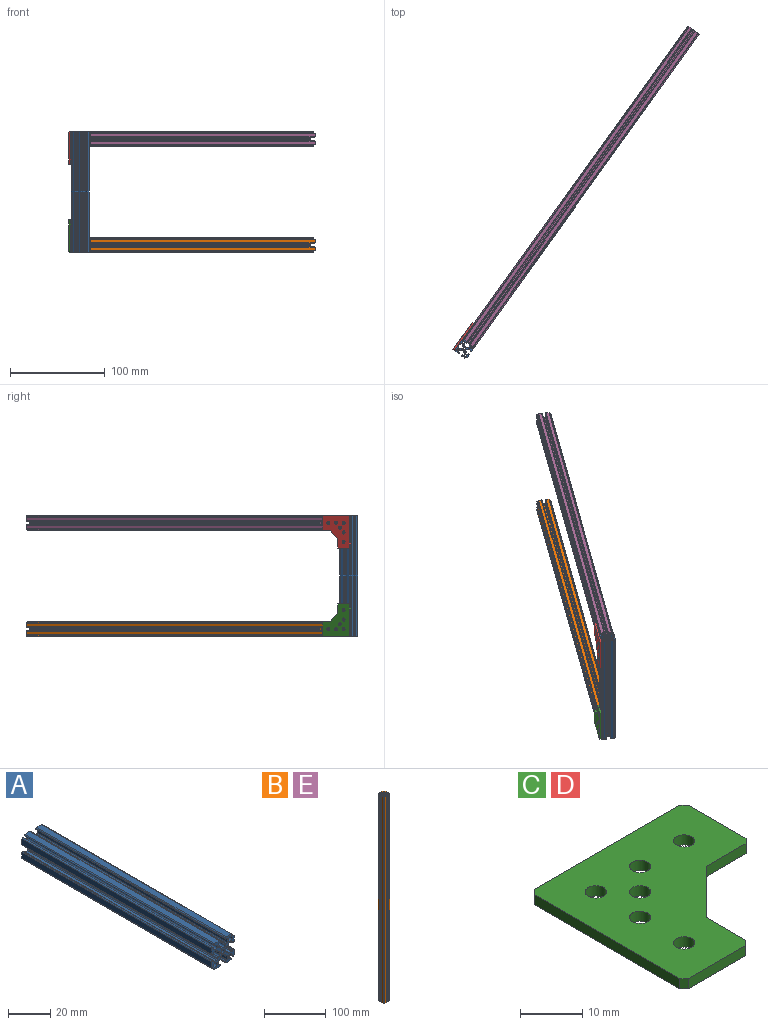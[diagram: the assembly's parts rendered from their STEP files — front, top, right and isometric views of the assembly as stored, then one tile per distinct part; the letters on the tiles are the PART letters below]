
ASSEMBLY  parts=5 mates=12
PART A: 115 faces, bbox 15x127x15 mm
  f0: plane 127x3.34mm, normal (1,0,0), area 423.7mm2, adj f23,f70,f112,f114
  f1: plane 127x3.34mm, normal (0,0,-1), area 423.7mm2, adj f16,f23,f77,f114
  f2: plane 127x3.34mm, normal (-1,0,0), area 423.7mm2, adj f23,f58,f109,f114
  f3: plane 127x3.34mm, normal (0,0,1), area 423.7mm2, adj f23,f65,f111,f114
  f4: plane 127x3.34mm, normal (-1,0,0), area 423.7mm2, adj f23,f62,f113,f114
  f5: plane 127x3.34mm, normal (0,0,-1), area 423.7mm2, adj f17,f23,f73,f114
  f6: plane 127x3.34mm, normal (1,0,0), area 423.7mm2, adj f23,f69,f110,f114
  f7: plane 127x3.34mm, normal (0,0,1), area 423.7mm2, adj f23,f63,f108,f114
  f8: plane 127x0.2mm, normal (-1,0,0), area 25.4mm2, adj f23,f65,f66,f114
  f9: plane 127x0.2mm, normal (1,0,0), area 25.4mm2, adj f23,f63,f64,f114
  f10: plane 127x0.2mm, normal (0,0,-1), area 25.4mm2, adj f23,f58,f59,f114
  f11: plane 127x0.2mm, normal (0,0,1), area 25.4mm2, adj f23,f61,f62,f114
  f12: plane 127x0.2mm, normal (1,0,0), area 25.4mm2, adj f23,f76,f77,f114
  f13: plane 127x0.2mm, normal (-1,0,0), area 25.4mm2, adj f23,f73,f74,f114
  f14: plane 127x0.2mm, normal (0,0,1), area 25.4mm2, adj f23,f70,f71,f114
  f15: plane 127x0.2mm, normal (0,0,-1), area 25.4mm2, adj f23,f68,f69,f114
  f16: cylinder r=0.5mm len=127mm, axis (0,1,0), area 149.6mm2, adj f1,f23,f53,f114
  f17: cylinder r=0.5mm len=127mm, axis (0,-1,0), area 149.6mm2, adj f5,f23,f102,f114
  f18: cylinder r=1.25mm len=127mm, axis (0,1,0), area 866.8mm2, adj f23,f104,f105,f114
  f19: cylinder r=1.25mm len=127mm, axis (0,1,0), area 866.8mm2, adj f23,f106,f107,f114
  f20: cylinder r=1.25mm len=127mm, axis (0,1,0), area 866.8mm2, adj f23,f52,f53,f114
  f21: cylinder r=1.25mm len=127mm, axis (0,1,0), area 866.8mm2, adj f23,f102,f103,f114
  f22: cylinder r=1.25mm len=127mm, axis (0,-1,0), area 997.5mm2, adj f23,f114
  f23: plane 15x15mm, normal (0,1,0), area 90.8mm2, adj f0,f1,f2,f3,f4,f5,f6,f7
  f24: plane 127x0.25mm, normal (0,0,1), area 31.8mm2, adj f23,f55,f80,f114
  f25: plane 127x1.2mm, normal (0,0,1), area 152.4mm2, adj f23,f86,f87,f114
  f26: plane 127x0.25mm, normal (0,0,1), area 31.8mm2, adj f23,f67,f79,f114
  f27: plane 127x2.1mm, normal (-1,0,0), area 266.7mm2, adj f23,f67,f100,f114
  f28: plane 127x0.4mm, normal (0,0,-1), area 50.8mm2, adj f23,f66,f100,f114
  f29: plane 127x0.4mm, normal (0,0,-1), area 50.8mm2, adj f23,f64,f101,f114
  f30: plane 127x2.1mm, normal (1,0,0), area 266.7mm2, adj f23,f55,f101,f114
  f31: plane 127x0.25mm, normal (-1,0,0), area 31.8mm2, adj f23,f54,f81,f114
  f32: plane 127x1.2mm, normal (-1,0,0), area 152.4mm2, adj f23,f88,f89,f114
  f33: plane 127x0.25mm, normal (-1,0,0), area 31.8mm2, adj f23,f60,f78,f114
  f34: plane 127x2.1mm, normal (0,0,-1), area 266.7mm2, adj f23,f60,f94,f114
  f35: plane 127x0.4mm, normal (1,0,0), area 50.8mm2, adj f23,f59,f94,f114
  f36: plane 127x0.4mm, normal (1,0,0), area 50.8mm2, adj f23,f61,f95,f114
  f37: plane 127x2.1mm, normal (0,0,1), area 266.7mm2, adj f23,f54,f95,f114
  f38: plane 127x0.25mm, normal (0,0,-1), area 31.8mm2, adj f23,f57,f83,f114
  f39: plane 127x1.2mm, normal (0,0,-1), area 152.4mm2, adj f23,f90,f91,f114
  f40: plane 127x0.25mm, normal (0,0,-1), area 31.8mm2, adj f23,f75,f82,f114
  f41: plane 127x2.1mm, normal (1,0,0), area 266.7mm2, adj f23,f75,f96,f114
  f42: plane 127x0.4mm, normal (0,0,1), area 50.8mm2, adj f23,f76,f96,f114
  f43: plane 127x0.4mm, normal (0,0,1), area 50.8mm2, adj f23,f74,f97,f114
  f44: plane 127x2.1mm, normal (-1,0,0), area 266.7mm2, adj f23,f57,f97,f114
  f45: plane 127x0.25mm, normal (1,0,0), area 31.8mm2, adj f23,f56,f84,f114
  f46: plane 127x1.2mm, normal (1,0,0), area 152.4mm2, adj f23,f92,f93,f114
  f47: plane 127x0.25mm, normal (1,0,0), area 31.8mm2, adj f23,f72,f85,f114
  f48: plane 127x2.1mm, normal (0,0,1), area 266.7mm2, adj f23,f72,f98,f114
  f49: plane 127x0.4mm, normal (-1,0,0), area 50.8mm2, adj f23,f71,f98,f114
  f50: plane 127x0.4mm, normal (-1,0,0), area 50.8mm2, adj f23,f68,f99,f114
  f51: plane 127x2.1mm, normal (0,0,-1), area 266.7mm2, adj f23,f56,f99,f114
  f52: plane 127x0.48mm, normal (0.71,0,-0.71), area 86.7mm2, adj f20,f23,f113,f114
  f53: plane 127x0.48mm, normal (-0.71,0,0.71), area 86.7mm2, adj f16,f20,f23,f114
  f54: cylinder r=0.5mm len=127mm, axis (0,-1,0), area 99.7mm2, adj f23,f31,f37,f114
  f55: cylinder r=0.5mm len=127mm, axis (0,-1,0), area 99.7mm2, adj f23,f24,f30,f114
  f56: cylinder r=0.5mm len=127mm, axis (0,-1,0), area 99.7mm2, adj f23,f45,f51,f114
  f57: cylinder r=0.5mm len=127mm, axis (0,-1,0), area 99.7mm2, adj f23,f38,f44,f114
  f58: cylinder r=0.5mm len=127mm, axis (0,1,0), area 99.7mm2, adj f2,f10,f23,f114
  f59: cylinder r=0.5mm len=127mm, axis (0,1,0), area 99.7mm2, adj f10,f23,f35,f114
  f60: cylinder r=0.5mm len=127mm, axis (0,-1,0), area 99.7mm2, adj f23,f33,f34,f114
  f61: cylinder r=0.5mm len=127mm, axis (0,1,0), area 99.7mm2, adj f11,f23,f36,f114
  f62: cylinder r=0.5mm len=127mm, axis (0,1,0), area 99.7mm2, adj f4,f11,f23,f114
  f63: cylinder r=0.5mm len=127mm, axis (0,1,0), area 99.7mm2, adj f7,f9,f23,f114
  f64: cylinder r=0.5mm len=127mm, axis (0,1,0), area 99.7mm2, adj f9,f23,f29,f114
  f65: cylinder r=0.5mm len=127mm, axis (0,1,0), area 99.7mm2, adj f3,f8,f23,f114
  f66: cylinder r=0.5mm len=127mm, axis (0,1,0), area 99.7mm2, adj f8,f23,f28,f114
  f67: cylinder r=0.5mm len=127mm, axis (0,-1,0), area 99.7mm2, adj f23,f26,f27,f114
  f68: cylinder r=0.5mm len=127mm, axis (0,1,0), area 99.7mm2, adj f15,f23,f50,f114
  f69: cylinder r=0.5mm len=127mm, axis (0,1,0), area 99.7mm2, adj f6,f15,f23,f114
  f70: cylinder r=0.5mm len=127mm, axis (0,1,0), area 99.7mm2, adj f0,f14,f23,f114
  f71: cylinder r=0.5mm len=127mm, axis (0,1,0), area 99.7mm2, adj f14,f23,f49,f114
  f72: cylinder r=0.5mm len=127mm, axis (0,-1,0), area 99.7mm2, adj f23,f47,f48,f114
  f73: cylinder r=0.5mm len=127mm, axis (0,1,0), area 99.7mm2, adj f5,f13,f23,f114
  f74: cylinder r=0.5mm len=127mm, axis (0,1,0), area 99.7mm2, adj f13,f23,f43,f114
  f75: cylinder r=0.5mm len=127mm, axis (0,-1,0), area 99.7mm2, adj f23,f40,f41,f114
  f76: cylinder r=0.5mm len=127mm, axis (0,1,0), area 99.7mm2, adj f12,f23,f42,f114
  f77: cylinder r=0.5mm len=127mm, axis (0,1,0), area 99.7mm2, adj f1,f12,f23,f114
  f78: cylinder r=0.5mm len=127mm, axis (0,1,0), area 99.7mm2, adj f23,f33,f88,f114
  f79: cylinder r=0.5mm len=127mm, axis (0,1,0), area 99.7mm2, adj f23,f26,f86,f114
  f80: cylinder r=0.5mm len=127mm, axis (0,1,0), area 99.7mm2, adj f23,f24,f87,f114
  f81: cylinder r=0.5mm len=127mm, axis (0,1,0), area 99.7mm2, adj f23,f31,f89,f114
  f82: cylinder r=0.5mm len=127mm, axis (0,1,0), area 99.7mm2, adj f23,f40,f90,f114
  f83: cylinder r=0.5mm len=127mm, axis (0,1,0), area 99.7mm2, adj f23,f38,f91,f114
  f84: cylinder r=0.5mm len=127mm, axis (0,1,0), area 99.7mm2, adj f23,f45,f92,f114
  f85: cylinder r=0.5mm len=127mm, axis (0,1,0), area 99.7mm2, adj f23,f47,f93,f114
  f86: cylinder r=1mm len=127mm, axis (0,-1,0), area 199.5mm2, adj f23,f25,f79,f114
  f87: cylinder r=1mm len=127mm, axis (0,-1,0), area 199.5mm2, adj f23,f25,f80,f114
  f88: cylinder r=1mm len=127mm, axis (0,-1,0), area 199.5mm2, adj f23,f32,f78,f114
  f89: cylinder r=1mm len=127mm, axis (0,-1,0), area 199.5mm2, adj f23,f32,f81,f114
  f90: cylinder r=1mm len=127mm, axis (0,-1,0), area 199.5mm2, adj f23,f39,f82,f114
  f91: cylinder r=1mm len=127mm, axis (0,-1,0), area 199.5mm2, adj f23,f39,f83,f114
  f92: cylinder r=1mm len=127mm, axis (0,-1,0), area 199.5mm2, adj f23,f46,f84,f114
  f93: cylinder r=1mm len=127mm, axis (0,-1,0), area 199.5mm2, adj f23,f46,f85,f114
  f94: cylinder r=0.2mm len=127mm, axis (0,-1,0), area 39.9mm2, adj f23,f34,f35,f114
  f95: cylinder r=0.2mm len=127mm, axis (0,-1,0), area 39.9mm2, adj f23,f36,f37,f114
  f96: cylinder r=0.2mm len=127mm, axis (0,-1,0), area 39.9mm2, adj f23,f41,f42,f114
  f97: cylinder r=0.2mm len=127mm, axis (0,-1,0), area 39.9mm2, adj f23,f43,f44,f114
  f98: cylinder r=0.2mm len=127mm, axis (0,-1,0), area 39.9mm2, adj f23,f48,f49,f114
  f99: cylinder r=0.2mm len=127mm, axis (0,-1,0), area 39.9mm2, adj f23,f50,f51,f114
  f100: cylinder r=0.2mm len=127mm, axis (0,-1,0), area 39.9mm2, adj f23,f27,f28,f114
  f101: cylinder r=0.2mm len=127mm, axis (0,-1,0), area 39.9mm2, adj f23,f29,f30,f114
  f102: plane 127x0.48mm, normal (0.71,0,0.71), area 86.7mm2, adj f17,f21,f23,f114
  f103: plane 127x0.48mm, normal (-0.71,0,-0.71), area 86.7mm2, adj f21,f23,f112,f114
  f104: plane 127x0.48mm, normal (-0.71,0,0.71), area 86.7mm2, adj f18,f23,f110,f114
  f105: plane 127x0.48mm, normal (0.71,0,-0.71), area 86.7mm2, adj f18,f23,f111,f114
  f106: plane 127x0.48mm, normal (-0.71,0,-0.71), area 86.7mm2, adj f19,f23,f108,f114
  f107: plane 127x0.48mm, normal (0.71,0,0.71), area 86.7mm2, adj f19,f23,f109,f114
  f108: cylinder r=0.5mm len=127mm, axis (0,-1,0), area 149.6mm2, adj f7,f23,f106,f114
  f109: cylinder r=0.5mm len=127mm, axis (0,1,0), area 149.6mm2, adj f2,f23,f107,f114
  f110: cylinder r=0.5mm len=127mm, axis (0,-1,0), area 149.6mm2, adj f6,f23,f104,f114
  f111: cylinder r=0.5mm len=127mm, axis (0,1,0), area 149.6mm2, adj f3,f23,f105,f114
  f112: cylinder r=0.5mm len=127mm, axis (0,1,0), area 149.6mm2, adj f0,f23,f103,f114
  f113: cylinder r=0.5mm len=127mm, axis (0,-1,0), area 149.6mm2, adj f4,f23,f52,f114
  f114: plane 15x15mm, normal (0,-1,0), area 90.8mm2, adj f0,f1,f2,f3,f4,f5,f6,f7
PART B: 115 faces, bbox 15x15x406.4 mm
  f0: plane 406.4x3.34mm, normal (1,0,0), area 1355.7mm2, adj f23,f70,f112,f114
  f1: plane 406.4x3.34mm, normal (0,-1,0), area 1355.7mm2, adj f16,f23,f77,f114
  f2: plane 406.4x3.34mm, normal (-1,0,0), area 1355.7mm2, adj f23,f58,f109,f114
  f3: plane 406.4x3.34mm, normal (0,1,0), area 1355.7mm2, adj f23,f65,f111,f114
  f4: plane 406.4x3.34mm, normal (-1,0,0), area 1355.7mm2, adj f23,f62,f113,f114
  f5: plane 406.4x3.34mm, normal (0,-1,0), area 1355.7mm2, adj f17,f23,f73,f114
  f6: plane 406.4x3.34mm, normal (1,0,0), area 1355.7mm2, adj f23,f69,f110,f114
  f7: plane 406.4x3.34mm, normal (0,1,0), area 1355.7mm2, adj f23,f63,f108,f114
  f8: plane 406.4x0.2mm, normal (-1,0,0), area 81.3mm2, adj f23,f65,f66,f114
  f9: plane 406.4x0.2mm, normal (1,0,0), area 81.3mm2, adj f23,f63,f64,f114
  f10: plane 406.4x0.2mm, normal (0,-1,0), area 81.3mm2, adj f23,f58,f59,f114
  f11: plane 406.4x0.2mm, normal (0,1,0), area 81.3mm2, adj f23,f61,f62,f114
  f12: plane 406.4x0.2mm, normal (1,0,0), area 81.3mm2, adj f23,f76,f77,f114
  f13: plane 406.4x0.2mm, normal (-1,0,0), area 81.3mm2, adj f23,f73,f74,f114
  f14: plane 406.4x0.2mm, normal (0,1,0), area 81.3mm2, adj f23,f70,f71,f114
  f15: plane 406.4x0.2mm, normal (0,-1,0), area 81.3mm2, adj f23,f68,f69,f114
  f16: cylinder r=0.5mm len=406.4mm, axis (0,0,-1), area 478.8mm2, adj f1,f23,f53,f114
  f17: cylinder r=0.5mm len=406.4mm, axis (0,0,1), area 478.8mm2, adj f5,f23,f102,f114
  f18: cylinder r=1.25mm len=406.4mm, axis (0,0,-1), area 2773.8mm2, adj f23,f104,f105,f114
  f19: cylinder r=1.25mm len=406.4mm, axis (0,0,-1), area 2773.8mm2, adj f23,f106,f107,f114
  f20: cylinder r=1.25mm len=406.4mm, axis (0,0,-1), area 2773.8mm2, adj f23,f52,f53,f114
  f21: cylinder r=1.25mm len=406.4mm, axis (0,0,-1), area 2773.8mm2, adj f23,f102,f103,f114
  f22: cylinder r=1.25mm len=406.4mm, axis (0,0,1), area 3191.9mm2, adj f23,f114
  f23: plane 15x15mm, normal (0,0,-1), area 90.8mm2, adj f0,f1,f2,f3,f4,f5,f6,f7
  f24: plane 406.4x0.25mm, normal (0,1,0), area 101.6mm2, adj f23,f55,f80,f114
  f25: plane 406.4x1.2mm, normal (0,1,0), area 487.7mm2, adj f23,f86,f87,f114
  f26: plane 406.4x0.25mm, normal (0,1,0), area 101.6mm2, adj f23,f67,f79,f114
  f27: plane 406.4x2.1mm, normal (-1,0,0), area 853.4mm2, adj f23,f67,f100,f114
  f28: plane 406.4x0.4mm, normal (0,-1,0), area 162.6mm2, adj f23,f66,f100,f114
  f29: plane 406.4x0.4mm, normal (0,-1,0), area 162.6mm2, adj f23,f64,f101,f114
  f30: plane 406.4x2.1mm, normal (1,0,0), area 853.4mm2, adj f23,f55,f101,f114
  f31: plane 406.4x0.25mm, normal (-1,0,0), area 101.6mm2, adj f23,f54,f81,f114
  f32: plane 406.4x1.2mm, normal (-1,0,0), area 487.7mm2, adj f23,f88,f89,f114
  f33: plane 406.4x0.25mm, normal (-1,0,0), area 101.6mm2, adj f23,f60,f78,f114
  f34: plane 406.4x2.1mm, normal (0,-1,0), area 853.4mm2, adj f23,f60,f94,f114
  f35: plane 406.4x0.4mm, normal (1,0,0), area 162.6mm2, adj f23,f59,f94,f114
  f36: plane 406.4x0.4mm, normal (1,0,0), area 162.6mm2, adj f23,f61,f95,f114
  f37: plane 406.4x2.1mm, normal (0,1,0), area 853.4mm2, adj f23,f54,f95,f114
  f38: plane 406.4x0.25mm, normal (0,-1,0), area 101.6mm2, adj f23,f57,f83,f114
  f39: plane 406.4x1.2mm, normal (0,-1,0), area 487.7mm2, adj f23,f90,f91,f114
  f40: plane 406.4x0.25mm, normal (0,-1,0), area 101.6mm2, adj f23,f75,f82,f114
  f41: plane 406.4x2.1mm, normal (1,0,0), area 853.4mm2, adj f23,f75,f96,f114
  f42: plane 406.4x0.4mm, normal (0,1,0), area 162.6mm2, adj f23,f76,f96,f114
  f43: plane 406.4x0.4mm, normal (0,1,0), area 162.6mm2, adj f23,f74,f97,f114
  f44: plane 406.4x2.1mm, normal (-1,0,0), area 853.4mm2, adj f23,f57,f97,f114
  f45: plane 406.4x0.25mm, normal (1,0,0), area 101.6mm2, adj f23,f56,f84,f114
  f46: plane 406.4x1.2mm, normal (1,0,0), area 487.7mm2, adj f23,f92,f93,f114
  f47: plane 406.4x0.25mm, normal (1,0,0), area 101.6mm2, adj f23,f72,f85,f114
  f48: plane 406.4x2.1mm, normal (0,1,0), area 853.4mm2, adj f23,f72,f98,f114
  f49: plane 406.4x0.4mm, normal (-1,0,0), area 162.6mm2, adj f23,f71,f98,f114
  f50: plane 406.4x0.4mm, normal (-1,0,0), area 162.6mm2, adj f23,f68,f99,f114
  f51: plane 406.4x2.1mm, normal (0,-1,0), area 853.4mm2, adj f23,f56,f99,f114
  f52: plane 406.4x0.48mm, normal (0.71,-0.71,0), area 277.5mm2, adj f20,f23,f113,f114
  f53: plane 406.4x0.48mm, normal (-0.71,0.71,0), area 277.5mm2, adj f16,f20,f23,f114
  f54: cylinder r=0.5mm len=406.4mm, axis (0,0,1), area 319.2mm2, adj f23,f31,f37,f114
  f55: cylinder r=0.5mm len=406.4mm, axis (0,0,1), area 319.2mm2, adj f23,f24,f30,f114
  f56: cylinder r=0.5mm len=406.4mm, axis (0,0,1), area 319.2mm2, adj f23,f45,f51,f114
  f57: cylinder r=0.5mm len=406.4mm, axis (0,0,1), area 319.2mm2, adj f23,f38,f44,f114
  f58: cylinder r=0.5mm len=406.4mm, axis (0,0,-1), area 319.2mm2, adj f2,f10,f23,f114
  f59: cylinder r=0.5mm len=406.4mm, axis (0,0,-1), area 319.2mm2, adj f10,f23,f35,f114
  f60: cylinder r=0.5mm len=406.4mm, axis (0,0,1), area 319.2mm2, adj f23,f33,f34,f114
  f61: cylinder r=0.5mm len=406.4mm, axis (0,0,-1), area 319.2mm2, adj f11,f23,f36,f114
  f62: cylinder r=0.5mm len=406.4mm, axis (0,0,-1), area 319.2mm2, adj f4,f11,f23,f114
  f63: cylinder r=0.5mm len=406.4mm, axis (0,0,-1), area 319.2mm2, adj f7,f9,f23,f114
  f64: cylinder r=0.5mm len=406.4mm, axis (0,0,-1), area 319.2mm2, adj f9,f23,f29,f114
  f65: cylinder r=0.5mm len=406.4mm, axis (0,0,-1), area 319.2mm2, adj f3,f8,f23,f114
  f66: cylinder r=0.5mm len=406.4mm, axis (0,0,-1), area 319.2mm2, adj f8,f23,f28,f114
  f67: cylinder r=0.5mm len=406.4mm, axis (0,0,1), area 319.2mm2, adj f23,f26,f27,f114
  f68: cylinder r=0.5mm len=406.4mm, axis (0,0,-1), area 319.2mm2, adj f15,f23,f50,f114
  f69: cylinder r=0.5mm len=406.4mm, axis (0,0,-1), area 319.2mm2, adj f6,f15,f23,f114
  f70: cylinder r=0.5mm len=406.4mm, axis (0,0,-1), area 319.2mm2, adj f0,f14,f23,f114
  f71: cylinder r=0.5mm len=406.4mm, axis (0,0,-1), area 319.2mm2, adj f14,f23,f49,f114
  f72: cylinder r=0.5mm len=406.4mm, axis (0,0,1), area 319.2mm2, adj f23,f47,f48,f114
  f73: cylinder r=0.5mm len=406.4mm, axis (0,0,-1), area 319.2mm2, adj f5,f13,f23,f114
  f74: cylinder r=0.5mm len=406.4mm, axis (0,0,-1), area 319.2mm2, adj f13,f23,f43,f114
  f75: cylinder r=0.5mm len=406.4mm, axis (0,0,1), area 319.2mm2, adj f23,f40,f41,f114
  f76: cylinder r=0.5mm len=406.4mm, axis (0,0,-1), area 319.2mm2, adj f12,f23,f42,f114
  f77: cylinder r=0.5mm len=406.4mm, axis (0,0,-1), area 319.2mm2, adj f1,f12,f23,f114
  f78: cylinder r=0.5mm len=406.4mm, axis (0,0,-1), area 319.2mm2, adj f23,f33,f88,f114
  f79: cylinder r=0.5mm len=406.4mm, axis (0,0,-1), area 319.2mm2, adj f23,f26,f86,f114
  f80: cylinder r=0.5mm len=406.4mm, axis (0,0,-1), area 319.2mm2, adj f23,f24,f87,f114
  f81: cylinder r=0.5mm len=406.4mm, axis (0,0,-1), area 319.2mm2, adj f23,f31,f89,f114
  f82: cylinder r=0.5mm len=406.4mm, axis (0,0,-1), area 319.2mm2, adj f23,f40,f90,f114
  f83: cylinder r=0.5mm len=406.4mm, axis (0,0,-1), area 319.2mm2, adj f23,f38,f91,f114
  f84: cylinder r=0.5mm len=406.4mm, axis (0,0,-1), area 319.2mm2, adj f23,f45,f92,f114
  f85: cylinder r=0.5mm len=406.4mm, axis (0,0,-1), area 319.2mm2, adj f23,f47,f93,f114
  f86: cylinder r=1mm len=406.4mm, axis (0,0,1), area 638.4mm2, adj f23,f25,f79,f114
  f87: cylinder r=1mm len=406.4mm, axis (0,0,1), area 638.4mm2, adj f23,f25,f80,f114
  f88: cylinder r=1mm len=406.4mm, axis (0,0,1), area 638.4mm2, adj f23,f32,f78,f114
  f89: cylinder r=1mm len=406.4mm, axis (0,0,1), area 638.4mm2, adj f23,f32,f81,f114
  f90: cylinder r=1mm len=406.4mm, axis (0,0,1), area 638.4mm2, adj f23,f39,f82,f114
  f91: cylinder r=1mm len=406.4mm, axis (0,0,1), area 638.4mm2, adj f23,f39,f83,f114
  f92: cylinder r=1mm len=406.4mm, axis (0,0,1), area 638.4mm2, adj f23,f46,f84,f114
  f93: cylinder r=1mm len=406.4mm, axis (0,0,1), area 638.4mm2, adj f23,f46,f85,f114
  f94: cylinder r=0.2mm len=406.4mm, axis (0,0,1), area 127.7mm2, adj f23,f34,f35,f114
  f95: cylinder r=0.2mm len=406.4mm, axis (0,0,1), area 127.7mm2, adj f23,f36,f37,f114
  f96: cylinder r=0.2mm len=406.4mm, axis (0,0,1), area 127.7mm2, adj f23,f41,f42,f114
  f97: cylinder r=0.2mm len=406.4mm, axis (0,0,1), area 127.7mm2, adj f23,f43,f44,f114
  f98: cylinder r=0.2mm len=406.4mm, axis (0,0,1), area 127.7mm2, adj f23,f48,f49,f114
  f99: cylinder r=0.2mm len=406.4mm, axis (0,0,1), area 127.7mm2, adj f23,f50,f51,f114
  f100: cylinder r=0.2mm len=406.4mm, axis (0,0,1), area 127.7mm2, adj f23,f27,f28,f114
  f101: cylinder r=0.2mm len=406.4mm, axis (0,0,1), area 127.7mm2, adj f23,f29,f30,f114
  f102: plane 406.4x0.48mm, normal (0.71,0.71,0), area 277.5mm2, adj f17,f21,f23,f114
  f103: plane 406.4x0.48mm, normal (-0.71,-0.71,0), area 277.5mm2, adj f21,f23,f112,f114
  f104: plane 406.4x0.48mm, normal (-0.71,0.71,0), area 277.5mm2, adj f18,f23,f110,f114
  f105: plane 406.4x0.48mm, normal (0.71,-0.71,0), area 277.5mm2, adj f18,f23,f111,f114
  f106: plane 406.4x0.48mm, normal (-0.71,-0.71,0), area 277.5mm2, adj f19,f23,f108,f114
  f107: plane 406.4x0.48mm, normal (0.71,0.71,0), area 277.5mm2, adj f19,f23,f109,f114
  f108: cylinder r=0.5mm len=406.4mm, axis (0,0,1), area 478.8mm2, adj f7,f23,f106,f114
  f109: cylinder r=0.5mm len=406.4mm, axis (0,0,-1), area 478.8mm2, adj f2,f23,f107,f114
  f110: cylinder r=0.5mm len=406.4mm, axis (0,0,1), area 478.8mm2, adj f6,f23,f104,f114
  f111: cylinder r=0.5mm len=406.4mm, axis (0,0,-1), area 478.8mm2, adj f3,f23,f105,f114
  f112: cylinder r=0.5mm len=406.4mm, axis (0,0,-1), area 478.8mm2, adj f0,f23,f103,f114
  f113: cylinder r=0.5mm len=406.4mm, axis (0,0,1), area 478.8mm2, adj f4,f23,f52,f114
  f114: plane 15x15mm, normal (0,0,1), area 90.8mm2, adj f0,f1,f2,f3,f4,f5,f6,f7
PART C: 20 faces, bbox 35x35x2 mm
  f0: cylinder r=1.7mm len=3.4mm, axis (0,0,1), area 21.4mm2, adj f7,f8
  f1: cylinder r=1.7mm len=3.4mm, axis (0,0,-1), area 21.4mm2, adj f7,f8
  f2: cylinder r=1.7mm len=3.4mm, axis (0,0,-1), area 21.4mm2, adj f7,f8
  f3: cylinder r=1.7mm len=3.4mm, axis (0,0,-1), area 21.4mm2, adj f7,f8
  f4: cylinder r=1.7mm len=3.4mm, axis (0,0,-1), area 21.4mm2, adj f7,f8
  f5: cylinder r=1.7mm len=3.4mm, axis (0,0,-1), area 21.4mm2, adj f7,f8
  f6: plane 9x2mm, normal (1,0,0), area 18mm2, adj f7,f8,f14,f19
  f7: plane 35x35mm, normal (0,0,1), area 818mm2, adj f0,f1,f2,f3,f4,f5,f6,f9
  f8: plane 35x35mm, normal (0,0,-1), area 818mm2, adj f0,f1,f2,f3,f4,f5,f6,f9
  f9: plane 33x2mm, normal (0,1,0), area 66mm2, adj f7,f8,f15,f17
  f10: plane 33x2mm, normal (-1,0,0), area 66mm2, adj f7,f8,f15,f18
  f11: plane 13x2mm, normal (0,-1,0), area 26mm2, adj f7,f8,f18,f19
  f12: plane 9x2mm, normal (0,-1,0), area 18mm2, adj f7,f8,f14,f16
  f13: plane 13x2mm, normal (1,0,0), area 26mm2, adj f7,f8,f16,f17
  f14: plane 10x10mm, normal (0.71,-0.71,0), area 28.3mm2, adj f6,f7,f8,f12
  f15: plane 2x1mm, normal (-0.71,0.71,0), area 2.8mm2, adj f7,f8,f9,f10
  f16: plane 2x1mm, normal (0.71,-0.71,0), area 2.8mm2, adj f7,f8,f12,f13
  f17: plane 2x1mm, normal (0.71,0.71,0), area 2.8mm2, adj f7,f8,f9,f13
  f18: plane 2x1mm, normal (-0.71,-0.71,0), area 2.8mm2, adj f7,f8,f10,f11
  f19: plane 2x1mm, normal (0.71,-0.71,0), area 2.8mm2, adj f6,f7,f8,f11
PART D: same geometry as C
PART E: same geometry as B
PLACE A rot(axis=(-0.91,0.29,-0.29),95.4deg) t=(-136.02,-449.2,119.03)mm
PLACE B rot(axis=(-0.91,0.29,-0.29),95.4deg) t=(-131.65,-443.1,126.53)mm
PLACE C rot(axis=(-0.81,-0.42,0.42),102deg) t=(-142.12,-444.82,126.53)mm
PLACE D rot(axis=(-0.69,0.22,0.69),155deg) t=(-142.12,-444.82,238.54)mm
PLACE E rot(axis=(-0.91,0.29,-0.29),95.4deg) t=(-131.65,-443.1,238.54)mm
MATE planar C.f10 <-> A.f1  axis (-0.58,-0.81,0) through (-147.3,-450.33,136.53)mm
MATE planar A.f2 <-> C.f5  axis (-0.81,0.58,0) through (-139.83,-441.64,182.54)mm
MATE planar A.f7 <-> E.f22  axis (0.58,0.81,0) through (-134.83,-440.82,182.54)mm
MATE planar A.f22 <-> B.f3  axis (0,0,-1) through (-136.02,-449.2,119.03)mm
MATE planar D.f10 <-> E.f1  axis (0,0,1) through (-137.1,-436.12,246.04)mm
MATE planar D.f0 <-> E.f2  axis (0.81,-0.58,0) through (-139.2,-440.76,233.54)mm
MATE planar E.f5 <-> A.f22  axis (0,0,1) through (-9.96,-280.32,246.04)mm
MATE planar B.f7 <-> C.f9  axis (0,0,-1) through (-16.33,-275.75,119.03)mm
MATE planar D.f1 <-> A.f2  axis (0.81,-0.58,0) through (-142.12,-444.82,218.54)mm
MATE planar A.f3 <-> B.f23  axis (0.58,0.81,0) through (-128.47,-445.39,182.54)mm
MATE planar D.f9 <-> A.f1  axis (-0.58,-0.81,0) through (-147.3,-450.33,228.54)mm
MATE planar A.f4 <-> B.f4  axis (-0.81,0.58,0) through (-144.4,-448.01,182.54)mm
